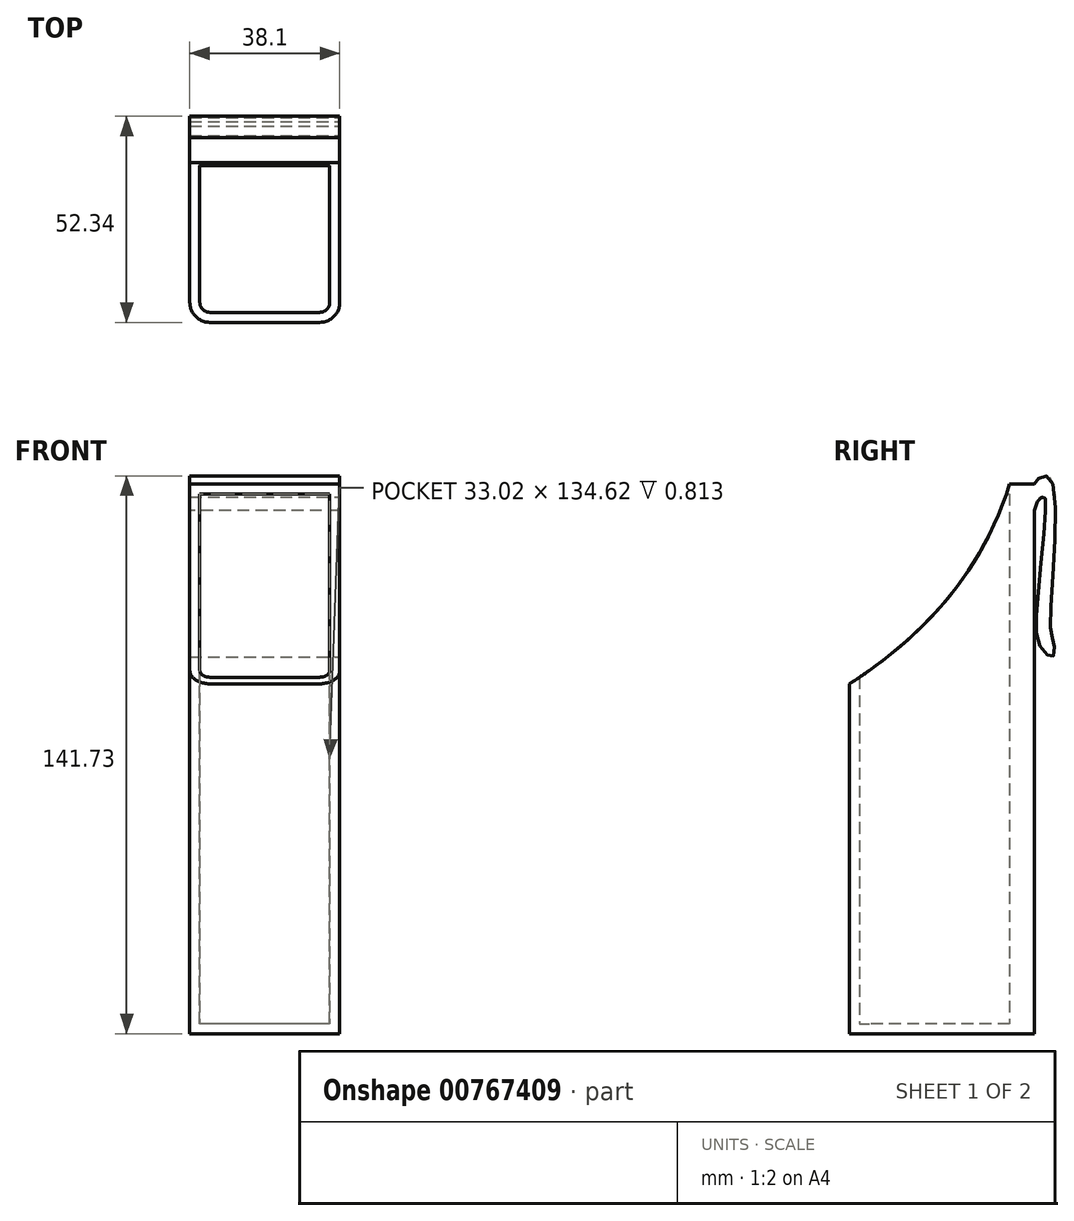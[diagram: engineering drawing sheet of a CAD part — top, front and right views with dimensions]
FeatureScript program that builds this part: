
annotation { "Feature Type Name" : "Feature", "Feature Type Description" : "" }
export const myFeature = defineFeature(function(context is Context, id is Id, definition is map)
    precondition{}
    {
        {
            var Q0;
            Q0=qCreatedBy(makeId("Right.planeOp"),FACE);
            var sketch = newSketch(context, id + "F0", { "sketchPlane" : qUnion([Q0])});
            skPoint(sketch, "E0.middle", {"position": v(0, 0) * mm});
            skLineSegment(sketch, "E1.bottom", {"start": v(0, -69.8) * mm, "end": v(-40.64, -69.8) * mm});
            skLineSegment(sketch, "E1.top", {"start": v(0, 19.1) * mm, "end": v(-40.64, 19.1) * mm});
            skLineSegment(sketch, "E1.left", {"start": v(0, -69.8) * mm, "end": v(0, 19.1) * mm});
            skLineSegment(sketch, "E1.right", {"start": v(-40.64, -69.8) * mm, "end": v(-40.64, 19.1) * mm});
            skLineSegment(sketch, "E2.bottom", {"start": v(0, -69.8) * mm, "end": v(6.35, -69.8) * mm});
            skLineSegment(sketch, "E2.top", {"start": v(0, 69.9) * mm, "end": v(6.35, 69.9) * mm});
            skLineSegment(sketch, "E2.left", {"start": v(0, -69.8) * mm, "end": v(0, 69.9) * mm});
            skLineSegment(sketch, "E2.right", {"start": v(6.35, -69.8) * mm, "end": v(6.35, 69.9) * mm});
            skFitSpline(sketch, "E3", {"points": [v(0, 69.9) * mm, v(-40.64, 19.1) * mm], "startDerivative": vector(-20.88, -69.1) * mm, "endDerivative": vector(-52.74, -33.72) * mm});
            skLineSegment(sketch, "E4", {"start": v(6.35, 69.9) * mm, "end": v(6.35, 67.44) * mm});
            skFitSpline(sketch, "E5", {"points": [v(6.35, 69.9) * mm, v(7.67, 71.4) * mm, v(10.49, 71.2) * mm, v(10.35, 34.98) * mm, v(11.2, 29.42) * mm, v(10.99, 26) * mm, v(8.17, 28) * mm, v(7.08, 40.2) * mm, v(9.08, 66.07) * mm, v(8.64, 66.5) * mm, v(7.61, 66.29) * mm, v(6.35, 63.08) * mm], "startDerivative": vector(18.7, 31.03) * mm, "endDerivative": vector(-18.39, -51.12) * mm});
            skSolve(sketch);
        }
        {
            var Q0;
            Q0 = qSketchRegion(id + "F0", true);
            extrude(context, id + "F1", {"entities" : qUnion([Q0]), "endBound" : BoundingType.SYMMETRIC, "depth" : 38.1 * mm, "offsetDistance" : 25.4 * mm});
        }
        {
            var Q0;
            Q0=makeQuery(id+"F1.opExtrude","CAP_EDGE",EDGE,{"disambiguationData":[OSD([sQuery(id+"F0.wireOp",EDGE,"E1.right")])],"isStart":false});
            fillet(context, id + "F2", {"entities" : qUnion([Q0]), "radius" : 5.08 * mm, "tangentPropagation" : true, "allowEdgeOverflow" : false});
        }
        {
            var Q0;
            Q0=makeQuery(id+"F1.opExtrude","CAP_EDGE",EDGE,{"disambiguationData":[OSD([sQuery(id+"F0.wireOp",EDGE,"E1.right")])],"isStart":true});
            fillet(context, id + "F3", {"entities" : qUnion([Q0]), "radius" : 5.08 * mm, "tangentPropagation" : true, "allowEdgeOverflow" : false});
        }
        {
            var Q0;
            Q0=makeQuery(id+"F1.opExtrude","SWEPT_FACE",FACE,{"disambiguationData":[OSD([sQuery(id+"F0.wireOp",EDGE,"E3")])]});
            shell(context, id + "F4", {"entities" : qUnion([Q0]), "thickness" : 2.54 * mm});
        }
        {
            var Q0;
            {var subQ3=sQuery(id+"F0.wireOp",EDGE,"E2.bottom");Q0=makeQuery(id+"F0.imprint","IMPRINT",FACE,{"disambiguationData":[TD([[makeQuery(id+"F0.imprint","IMPRINT",EDGE,{"derivedFrom":subQ3}),1.0]])]});}
            extrude(context, id + "F5", {"entities" : qUnion([Q0]), "operationType" : NewBodyOperationType.ADD, "endBound" : BoundingType.SYMMETRIC, "depth" : 38.1 * mm, "offsetDistance" : 25.4 * mm});
        }
    });
